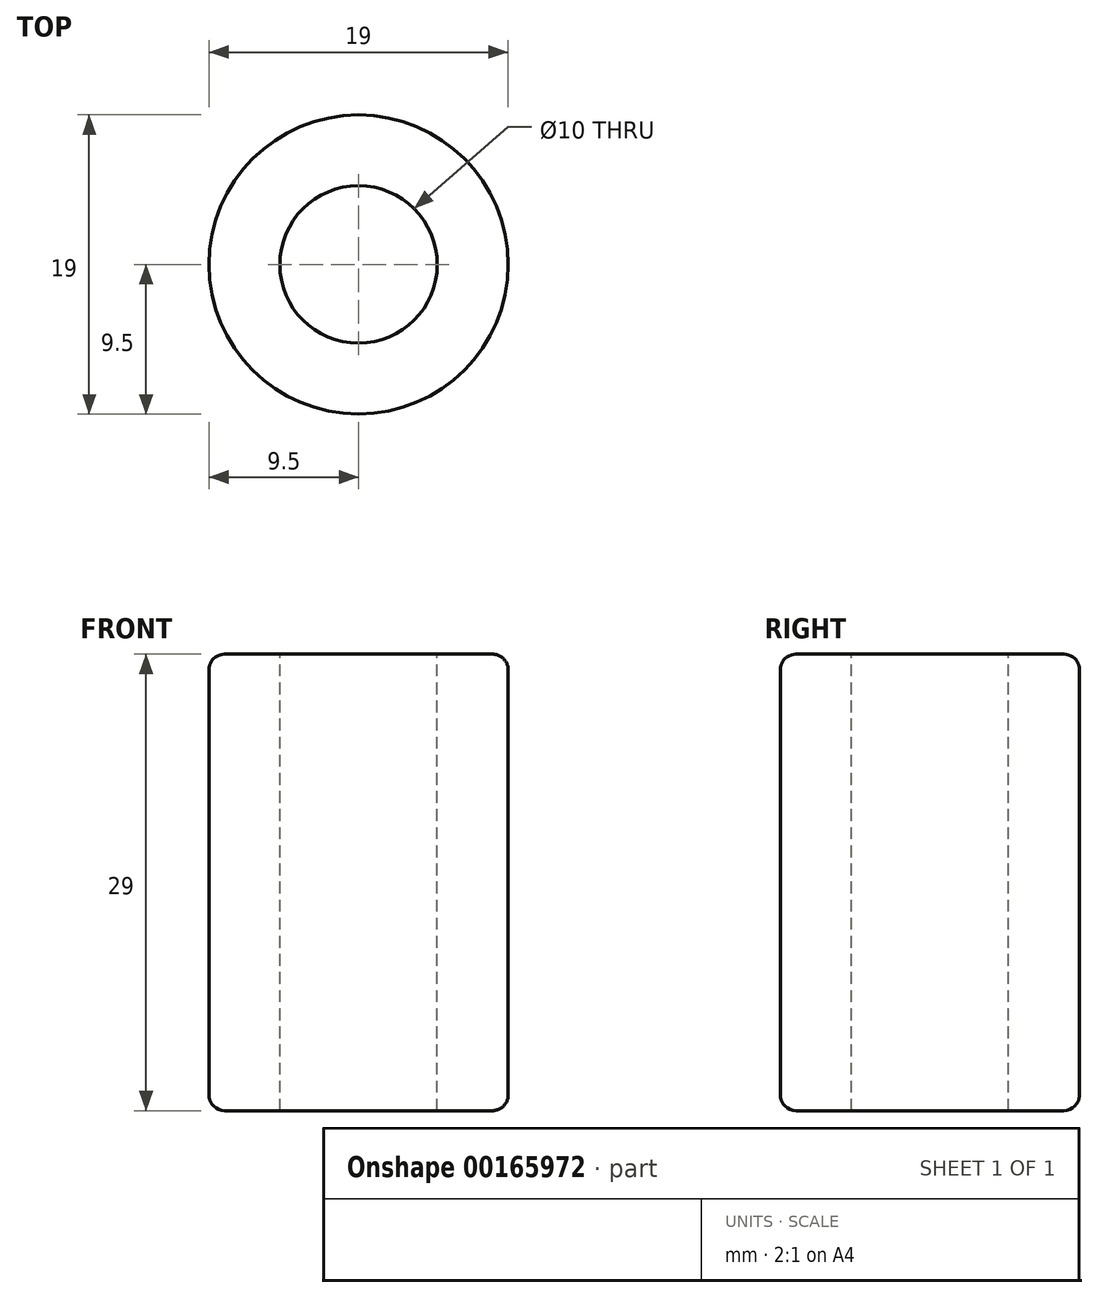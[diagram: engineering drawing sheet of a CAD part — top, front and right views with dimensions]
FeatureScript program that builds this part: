
annotation { "Feature Type Name" : "Feature", "Feature Type Description" : "" }
export const myFeature = defineFeature(function(context is Context, id is Id, definition is map)
    precondition{}
    {
        {
            var Q0;
            Q0=qCreatedBy(makeId("Top.planeOp"),FACE);
            var sketch = newSketch(context, id + "F0", { "sketchPlane" : qUnion([Q0])});
            skCircle(sketch, "E0", {"center": v(0, 0) * mm, "radius": 5 * mm});
            skCircle(sketch, "E1", {"center": v(0, 0) * mm, "radius": 9.5 * mm});
            skSolve(sketch);
        }
        {
            var Q0;
            Q0 = qSketchRegion(id + "F0", true);
            extrude(context, id + "F1", {"entities" : qUnion([Q0]), "flatOperationType" : FlatOperationType.REMOVE, "oppositeDirection" : true, "offsetDistance" : 25 * mm, "depth" : 29 * mm, "domain" : OperationDomain.MODEL});
        }
        {
            var Q0;
            Q0=makeQuery(id+"F1.opExtrude","CAP_EDGE",EDGE,{"disambiguationData":[OSD([sQuery(id+"F0.wireOp",EDGE,"E1")])],"isStart":true});
            var Q1;
            Q1=makeQuery(id+"F1.opExtrude","CAP_EDGE",EDGE,{"disambiguationData":[OSD([sQuery(id+"F0.wireOp",EDGE,"E1")])],"isStart":false});
            fillet(context, id + "F2", {"entities" : qUnion([Q0, Q1]), "radius" : 1 * mm, "tangentPropagation" : true, "allowEdgeOverflow" : false});
        }
    });
